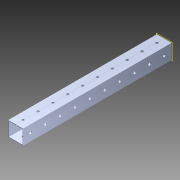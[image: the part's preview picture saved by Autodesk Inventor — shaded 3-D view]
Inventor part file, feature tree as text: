
AUTODESK INVENTOR PART (.ipt)
format: ipt  version: 2014 (Build 180170000, 170)  size: 1,167,872 bytes
history: native  units: in
note: dims shown in document units (in); Inventor stores cm internally (conversion verified against a paired STEP export)
features: pattern_circular x1, other x1, plane x1, extrude x1, imported_body x1, sketch x1
ambient origin geometry x8: Origin, YZ Plane, XZ Plane, XY Plane, X Axis, Y Axis, Z Axis, Center Point
bodies: Body1 (feature_tree)
feature tree (6):
  pattern_circular  "CirPattern2"
  other  "217-3426-STEP1"
  plane  "Work Plane1"
  extrude  "Extrusion1"  Depth=3937.0079in TaperAngle=0.0deg
  imported_body  "Base1"
  sketch  "Sketch1"  dims[d0=-10.0in d1=3937.0079in d2=0.0in]
